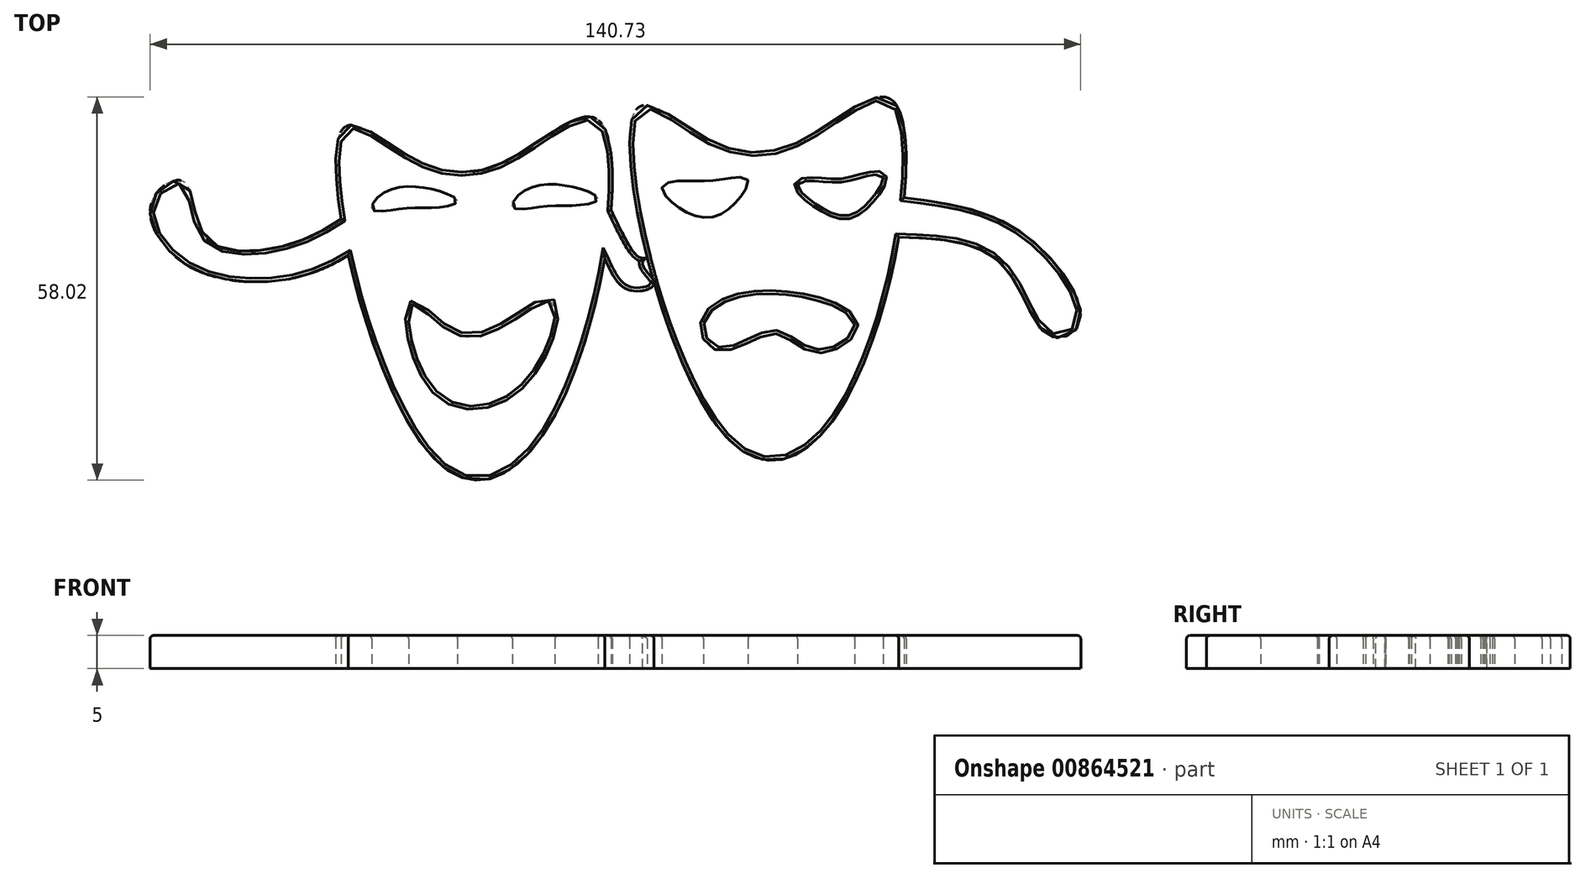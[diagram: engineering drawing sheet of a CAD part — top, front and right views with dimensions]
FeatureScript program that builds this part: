
annotation { "Feature Type Name" : "Feature", "Feature Type Description" : "" }
export const myFeature = defineFeature(function(context is Context, id is Id, definition is map)
    precondition{}
    {
        {
            var Q0;
            Q0=qCreatedBy(makeId("Top.planeOp"),FACE);
            var sketch = newSketch(context, id + "F0", { "sketchPlane" : qUnion([Q0])});
            skFitSpline(sketch, "E0", {"points": [v(-41.85, 42.36) * mm, v(-31.45, 38.14) * mm, v(-16.99, 37.65) * mm, v(-3.18, 43.82) * mm, v(-10.16, -1.68) * mm, v(-27.71, -7.7) * mm, v(-41.85, 42.36) * mm]});
            skFitSpline(sketch, "E1", {"points": [v(-36.55, 32.08) * mm, v(-30.45, 33.7) * mm, v(-24.44, 31.5) * mm, v(-28.18, 30.53) * mm, v(-32.24, 30.46) * mm, v(-37.28, 30.2) * mm, v(-36.55, 32.08) * mm]});
            skFitSpline(sketch, "E2", {"points": [v(-15.26, 32.4) * mm, v(-9.16, 34.03) * mm, v(-3.15, 31.83) * mm, v(-6.89, 30.86) * mm, v(-10.95, 30.78) * mm, v(-15.99, 30.53) * mm, v(-15.26, 32.4) * mm]});
            skFitSpline(sketch, "E3", {"points": [v(-31.27, 15.97) * mm, v(-22.96, 10.94) * mm, v(-10.4, 16.35) * mm, v(-14.36, 4.18) * mm, v(-27.89, 3.02) * mm, v(-31.27, 15.97) * mm]});
            skFitSpline(sketch, "E4", {"points": [v(2.58, 45.36) * mm, v(12.98, 41.14) * mm, v(27.44, 40.65) * mm, v(41.25, 46.82) * mm, v(34.27, 1.32) * mm, v(16.72, -4.7) * mm, v(2.58, 45.36) * mm]});
            skFitSpline(sketch, "E5", {"points": [v(37.06, 30.72) * mm, v(32.42, 29.66) * mm, v(27.02, 34.05) * mm, v(30.78, 34.5) * mm, v(34.65, 34.59) * mm, v(39.85, 35.35) * mm, v(37.06, 30.72) * mm]});
            skFitSpline(sketch, "E6", {"points": [v(18.41, 32.27) * mm, v(12.52, 29.08) * mm, v(6.49, 33.62) * mm, v(10.23, 34.6) * mm, v(14.29, 34.67) * mm, v(19.33, 34.92) * mm, v(18.41, 32.27) * mm]});
            skFitSpline(sketch, "E7", {"points": [v(12.8, 13.04) * mm, v(21.5, 17.49) * mm, v(35.61, 12.85) * mm, v(30, 9.08) * mm, v(23.53, 11.98) * mm, v(15.32, 9.37) * mm, v(12.8, 13.04) * mm]});
            skFitSpline(sketch, "E8", {"points": [v(-42.03, 28.82) * mm, v(-49.7, 25.02) * mm, v(-62.46, 25.99) * mm, v(-65.84, 34.5) * mm, v(-70.68, 31.4) * mm, v(-64.97, 21.64) * mm, v(-48.74, 20) * mm, v(-40.97, 23.32) * mm], "startDerivative": vector(-48.68, -31.65) * mm, "endDerivative": vector(51.14, 29.3) * mm});
            skFitSpline(sketch, "E9", {"points": [v(-1.22, 30.2) * mm, v(2.95, 23.1) * mm, v(4.25, 23) * mm], "startDerivative": vector(6.28, -13.4) * mm, "endDerivative": vector(4.4, 1.07) * mm});
            skFitSpline(sketch, "E10", {"points": [v(-2.17, 22.84) * mm, v(1.6, 18.07) * mm, v(5.26, 19.28) * mm, v(4.25, 23) * mm], "startDerivative": vector(8.01, -16.61) * mm, "endDerivative": vector(19.21, 9.32) * mm});
            skFitSpline(sketch, "E11", {"points": [v(43.1, 32.04) * mm, v(61.2, 26.51) * mm, v(69.67, 13.12) * mm, v(65.02, 11.2) * mm, v(57.92, 22) * mm, v(42.3, 26.08) * mm], "startDerivative": vector(78.77, -9.56) * mm, "endDerivative": vector(-81.96, 2.7) * mm});
            skSolve(sketch);
        }
        {
            var Q0;
            Q0=makeQuery(id+"F0.imprint","IMPRINT",FACE,{"disambiguationData":[TD([[makeQuery(id+"F0.imprint","IMPRINT",EDGE,{"derivedFrom":sQuery(id+"F0.wireOp",EDGE,"E1")}),1.0]])]});
            var Q1;
            {var subQ0=sQuery(id+"F0.wireOp",EDGE,"E8");Q1=makeQuery(id+"F0.imprint","IMPRINT",FACE,{"disambiguationData":[TD([[makeQuery(id+"F0.imprint","IMPRINT",EDGE,{"derivedFrom":subQ0}),1.0]])]});}
            var Q2;
            {var subQ5=sQuery(id+"F0.wireOp",EDGE,"E9");Q2=makeQuery(id+"F0.imprint","IMPRINT",FACE,{"disambiguationData":[TD([[makeQuery(id+"F0.imprint","IMPRINT",EDGE,{"derivedFrom":subQ5}),-1.0]])]});}
            var Q3;
            Q3=makeQuery(id+"F0.imprint","IMPRINT",FACE,{"disambiguationData":[TD([[makeQuery(id+"F0.imprint","IMPRINT",EDGE,{"derivedFrom":sQuery(id+"F0.wireOp",EDGE,"E5")}),1.0]])]});
            var Q4;
            {var subQ0=sQuery(id+"F0.wireOp",EDGE,"E11");Q4=makeQuery(id+"F0.imprint","IMPRINT",FACE,{"disambiguationData":[TD([[makeQuery(id+"F0.imprint","IMPRINT",EDGE,{"derivedFrom":subQ0}),-1.0]])]});}
            extrude(context, id + "F1", {"entities" : qUnion([Q0, Q1, Q2, Q3, Q4]), "depth" : 5 * mm, "offsetDistance" : 25 * mm});
        }
        {
            var Q0;
            Q0=makeQuery(id+"F1.opExtrude","CAP_FACE",FACE,{"disambiguationData":[OSD([sQuery(id+"F0.wireOp",EDGE,"E0"),sQuery(id+"F0.wireOp",EDGE,"E1"),sQuery(id+"F0.wireOp",EDGE,"E2"),sQuery(id+"F0.wireOp",EDGE,"E3"),sQuery(id+"F0.wireOp",EDGE,"E4"),sQuery(id+"F0.wireOp",EDGE,"E8"),sQuery(id+"F0.wireOp",EDGE,"E9"),sQuery(id+"F0.wireOp",EDGE,"E10")])],"isStart":false});
            var Q1;
            Q1=makeQuery(id+"F1.opExtrude","CAP_FACE",FACE,{"disambiguationData":[OSD([sQuery(id+"F0.wireOp",EDGE,"E4"),sQuery(id+"F0.wireOp",EDGE,"E5"),sQuery(id+"F0.wireOp",EDGE,"E6"),sQuery(id+"F0.wireOp",EDGE,"E7"),sQuery(id+"F0.wireOp",EDGE,"E10"),sQuery(id+"F0.wireOp",EDGE,"E11")])],"isStart":false});
            fillet(context, id + "F2", {"entities" : qUnion([Q0, Q1]), "radius" : 0.5 * mm, "tangentPropagation" : true, "allowEdgeOverflow" : false});
        }
    });
